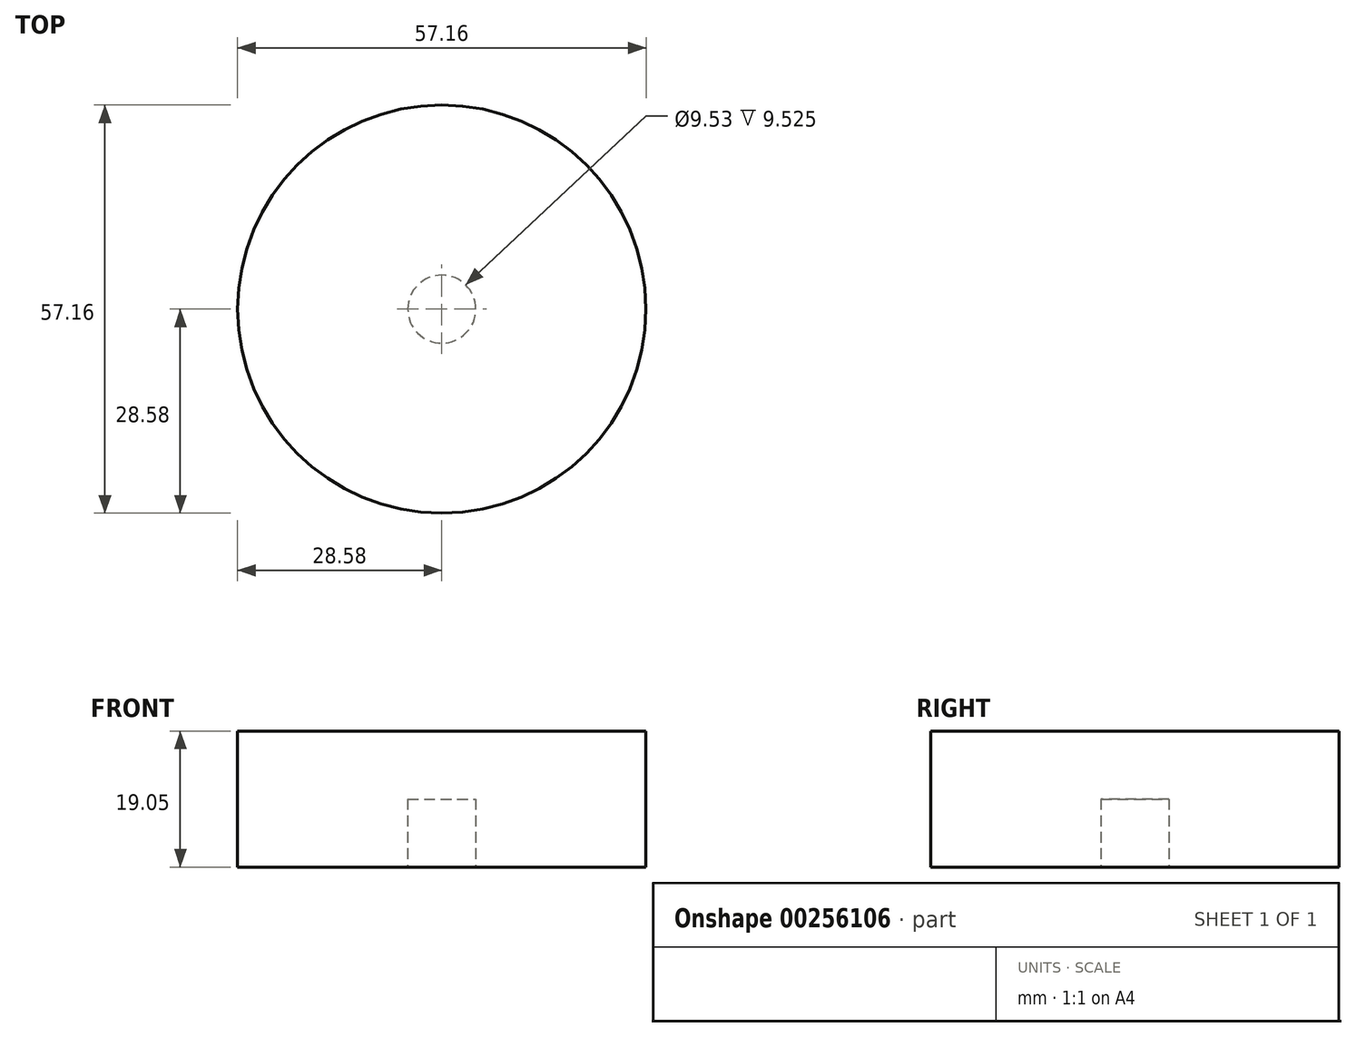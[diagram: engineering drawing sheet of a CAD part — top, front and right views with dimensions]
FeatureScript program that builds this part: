
annotation { "Feature Type Name" : "Feature", "Feature Type Description" : "" }
export const myFeature = defineFeature(function(context is Context, id is Id, definition is map)
    precondition{}
    {
        {
            var Q0;
            Q0=qCreatedBy(makeId("Top.planeOp"),FACE);
            var sketch = newSketch(context, id + "F0", { "sketchPlane" : qUnion([Q0])});
            skCircle(sketch, "E0", {"center": v(0, 0) * mm, "radius": 28.58 * mm});
            skSolve(sketch);
        }
        {
            var Q0;
            Q0 = qSketchRegion(id + "F0", true);
            extrude(context, id + "F1", {"entities" : qUnion([Q0]), "depth" : 19.05 * mm});
        }
        {
            var Q0;
            Q0=qCreatedBy(makeId("Top.planeOp"),FACE);
            var sketch = newSketch(context, id + "F2", { "sketchPlane" : qUnion([Q0])});
            skCircle(sketch, "E1", {"center": v(0, 0) * mm, "radius": 4.76 * mm});
            skSolve(sketch);
        }
        {
            var Q0;
            Q0 = qSketchRegion(id + "F2", true);
            extrude(context, id + "F3", {"entities" : qUnion([Q0]), "operationType" : NewBodyOperationType.ADD, "depth" : 9.52 * mm});
        }
        {
            var Q0;
            Q0=makeQuery(id+"F1.opExtrude","CAP_FACE",FACE,{"disambiguationData":[OSD([sQuery(id+"F0.wireOp",EDGE,"E0")])],"isStart":true});
            var sketch = newSketch(context, id + "F4", { "sketchPlane" : qUnion([Q0])});
            skCircle(sketch, "E2", {"center": v(0, 0) * mm, "radius": 4.76 * mm});
            skSolve(sketch);
        }
        {
            var Q0;
            Q0 = qSketchRegion(id + "F4", true);
            extrude(context, id + "F5", {"entities" : qUnion([Q0]), "operationType" : NewBodyOperationType.REMOVE, "oppositeDirection" : true, "depth" : 9.52 * mm});
        }
    });
